# Revit family: Electrical_Other-Electrical_Menzies-Metal_Electrical-Roof-Flashing (1)
name_source: partatom
category: Specialty Equipment
revit_build: Autodesk Revit 2018 (Build: 20170223_1515(x64)
units: mm (PartAtom-declared; Revit-internal decimal feet)

## family parameters
Cut with Voids When Loaded = No
Host = Face
OmniClass Number = 23.70.50.21.24.11
OmniClass Title = Roof Waste Water Drains
Part Type = Normal
Room Calculation Point = No
Round Connector Dimension = Use Diameter
Shared = No

## types (2) — shared parameters
Assembly Code = D2040200
CW Connection = No
Default Elevation = 48 "
Description = Electrical Roof Flashing
Drain Flow = 0 GPM
Edition number = 1
HW Connection = No
Manufacturer = Menzies Metal Products
Product Guid = 3b1ea523-ce04-4307-88be-b82241bbc6ef
Product Material = Metal - Menzies Metal Products - Aluminum
Product data url = https://www.bimobject.com
URL = https://www.menzies-metal.com
Vent Connection = No
Waste Connection = No

## per-type parameters (varying)
| type | Model | Pipe Height | Pipe diameter | Size | Weight |
| 2" | 600-1530 | 12 " | 2 " | Electrical_Other-Electrical_Menzies-Metal-Products_Electrical-Roof-Flashing : Type - (2in.) | 1.70 lbf |
| 3" | 600-1550 | 25 " | 3 " | Electrical_Other-Electrical_Menzies-Metal-Products_Electrical-Roof-Flashing : Type - (3in.) | 6.45 lbf |

## geometry (parser evidence)
native form markers: Sweep x5
no freeform markers — native parametric forms only
